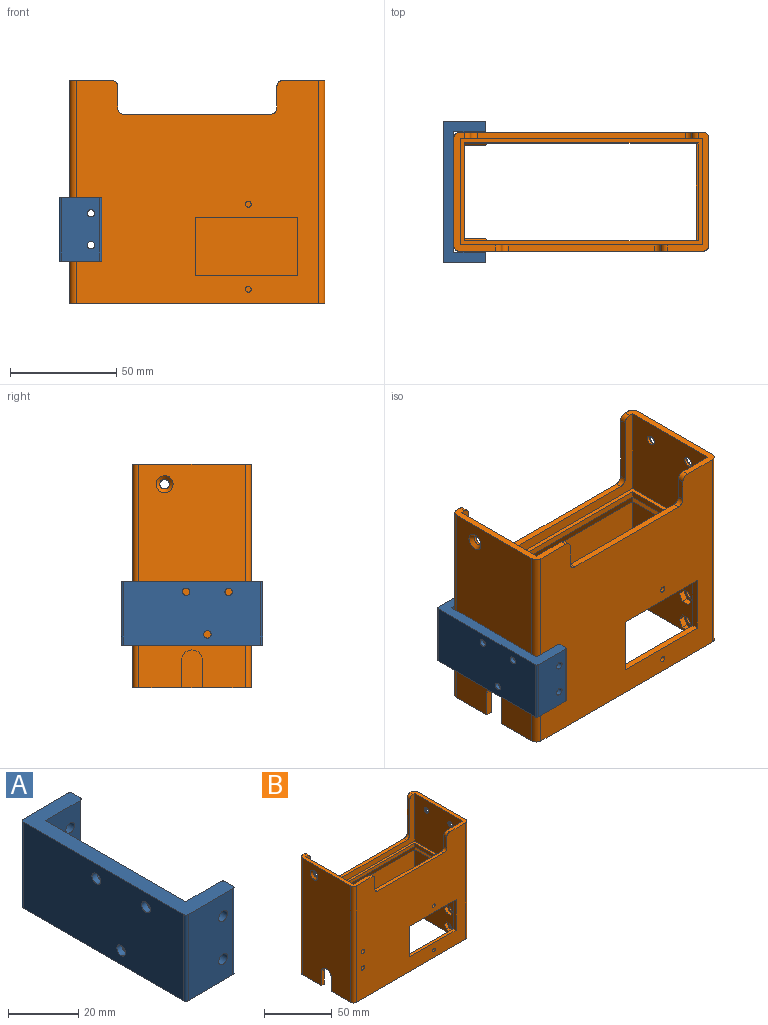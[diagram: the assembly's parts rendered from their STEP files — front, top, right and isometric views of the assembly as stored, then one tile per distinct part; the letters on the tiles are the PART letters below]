
ASSEMBLY  parts=2 mates=1
PART A: 44 faces, bbox 20x66.5x30 mm
  f0: cylinder r=1.75mm len=3.5mm, axis (-1,0,0), area 22mm2, adj f7,f27
  f1: cylinder r=1.75mm len=3.5mm, axis (-1,0,0), area 22mm2, adj f7,f20
  f2: cylinder r=1.75mm len=3.5mm, axis (-1,0,0), area 22mm2, adj f7,f13
  f3: plane 56.5x30mm, normal (1,0,0), area 1616.4mm2, adj f4,f10,f11,f12,f14,f15,f16,f17
  f4: plane 30x14mm, normal (0,-1,0), area 400.8mm2, adj f3,f11,f12,f36,f37,f38
  f5: plane 30x3mm, normal (1,0,0), area 90mm2, adj f11,f12,f38,f39
  f6: plane 30x18mm, normal (0,1,0), area 520.8mm2, adj f11,f12,f36,f37,f39,f40
  f7: plane 64.5x30mm, normal (-1,0,0), area 1906.1mm2, adj f0,f1,f2,f11,f12,f40,f41
  f8: plane 30x18mm, normal (0,-1,0), area 520.8mm2, adj f11,f12,f34,f35,f41,f42
  f9: plane 30x3mm, normal (1,0,0), area 90mm2, adj f11,f12,f42,f43
  f10: plane 30x14mm, normal (0,1,0), area 400.8mm2, adj f3,f11,f12,f34,f35,f43
  f11: plane 66.5x20mm, normal (0,0,1), area 481.2mm2, adj f3,f4,f5,f6,f7,f8,f9,f10
  f12: plane 66.5x20mm, normal (0,0,-1), area 481.2mm2, adj f3,f4,f5,f6,f7,f8,f9,f10
  f13: plane 6.35x5.5mm, normal (1,0,0), area 16.6mm2, adj f2,f14,f15,f16,f17,f18,f19
  f14: plane 3x2.75mm, normal (0,-0.87,-0.5), area 9.5mm2, adj f3,f13,f15,f19
  f15: plane 3.18x3mm, normal (0,0,-1), area 9.5mm2, adj f3,f13,f14,f16
  f16: plane 3x2.75mm, normal (0,0.87,-0.5), area 9.5mm2, adj f3,f13,f15,f17
  f17: plane 3x2.75mm, normal (0,0.87,0.5), area 9.5mm2, adj f3,f13,f16,f18
  f18: plane 3.18x3mm, normal (0,0,1), area 9.5mm2, adj f3,f13,f17,f19
  f19: plane 3x2.75mm, normal (0,-0.87,0.5), area 9.5mm2, adj f3,f13,f14,f18
  f20: plane 6.35x5.5mm, normal (1,0,0), area 16.6mm2, adj f1,f21,f22,f23,f24,f25,f26
  f21: plane 3x2.75mm, normal (0,-0.87,-0.5), area 9.5mm2, adj f3,f20,f22,f26
  f22: plane 3.18x3mm, normal (0,0,-1), area 9.5mm2, adj f3,f20,f21,f23
  f23: plane 3x2.75mm, normal (0,0.87,-0.5), area 9.5mm2, adj f3,f20,f22,f24
  f24: plane 3x2.75mm, normal (0,0.87,0.5), area 9.5mm2, adj f3,f20,f23,f25
  f25: plane 3.18x3mm, normal (0,0,1), area 9.5mm2, adj f3,f20,f24,f26
  f26: plane 3x2.75mm, normal (0,-0.87,0.5), area 9.5mm2, adj f3,f20,f21,f25
  f27: plane 6.35x5.5mm, normal (1,0,0), area 16.6mm2, adj f0,f28,f29,f30,f31,f32,f33
  f28: plane 3x2.75mm, normal (0,-0.87,-0.5), area 9.5mm2, adj f3,f27,f29,f33
  f29: plane 3.18x3mm, normal (0,0,-1), area 9.5mm2, adj f3,f27,f28,f30
  f30: plane 3x2.75mm, normal (0,0.87,-0.5), area 9.5mm2, adj f3,f27,f29,f31
  f31: plane 3x2.75mm, normal (0,0.87,0.5), area 9.5mm2, adj f3,f27,f30,f32
  f32: plane 3.18x3mm, normal (0,0,1), area 9.5mm2, adj f3,f27,f31,f33
  f33: plane 3x2.75mm, normal (0,-0.87,0.5), area 9.5mm2, adj f3,f27,f28,f32
  f34: cylinder r=1.75mm len=5mm, axis (0,-1,0), area 55mm2, adj f8,f10
  f35: cylinder r=1.75mm len=5mm, axis (0,-1,0), area 55mm2, adj f8,f10
  f36: cylinder r=1.75mm len=5mm, axis (0,-1,0), area 55mm2, adj f4,f6
  f37: cylinder r=1.75mm len=5mm, axis (0,-1,0), area 55mm2, adj f4,f6
  f38: cylinder r=1mm len=30mm, axis (0,0,-1), area 47.1mm2, adj f4,f5,f11,f12
  f39: cylinder r=1mm len=30mm, axis (0,0,1), area 47.1mm2, adj f5,f6,f11,f12
  f40: cylinder r=1mm len=30mm, axis (0,0,-1), area 47.1mm2, adj f6,f7,f11,f12
  f41: cylinder r=1mm len=30mm, axis (0,0,1), area 47.1mm2, adj f7,f8,f11,f12
  f42: cylinder r=1mm len=30mm, axis (0,0,1), area 47.1mm2, adj f8,f9,f11,f12
  f43: cylinder r=1mm len=30mm, axis (0,0,-1), area 47.1mm2, adj f9,f10,f11,f12
PART B: 131 faces, bbox 120x56x105 mm
  f0: cylinder r=2.25mm len=4.5mm, axis (1,0,0), area 42.4mm2, adj f25,f130
  f1: cylinder r=2.25mm len=4.5mm, axis (1,0,0), area 42.4mm2, adj f25,f123
  f2: cylinder r=2.25mm len=4.5mm, axis (1,0,0), area 42.4mm2, adj f25,f116
  f3: cylinder r=2.25mm len=4.5mm, axis (1,0,0), area 42.4mm2, adj f25,f109
  f4: cylinder r=1.75mm len=3.5mm, axis (0,-1,0), area 33mm2, adj f17,f96
  f5: cylinder r=1.75mm len=3.5mm, axis (0,-1,0), area 33mm2, adj f17,f89
  f6: cylinder r=1.75mm len=3.5mm, axis (0,-1,0), area 33mm2, adj f16,f82
  f7: cylinder r=1.75mm len=3.5mm, axis (0,-1,0), area 33mm2, adj f16,f75
  f8: plane 50x24.42mm, normal (-1,0,0), area 1220.9mm2, adj f9,f11,f21,f68
  f9: plane 114x54.42mm, normal (0,1,0), area 4032.1mm2, adj f8,f10,f26,f29,f32,f33,f34,f35
  f10: plane 54.42x50mm, normal (1,0,0), area 2263.6mm2, adj f9,f11,f18,f26,f46,f47,f48,f65
  f11: plane 114x54.42mm, normal (0,-1,0), area 5334.8mm2, adj f8,f10,f26,f31,f67,f68,f97,f98
  f12: plane 105x50mm, normal (-1,0,0), area 5033.4mm2, adj f15,f26,f46,f47,f48,f52,f62,f63
  f13: plane 56x19.6mm, normal (0,0,1), area 219.9mm2, adj f14,f16,f17,f22,f24,f25,f56,f57
  f14: plane 114x43mm, normal (0,1,0), area 3705.2mm2, adj f13,f15,f22,f23,f27,f41,f42,f43
  f15: plane 56x19.6mm, normal (0,0,1), area 219.9mm2, adj f12,f14,f16,f17,f23,f24,f53,f60
  f16: plane 114x105mm, normal (0,1,0), area 7866mm2, adj f6,f7,f13,f15,f26,f38,f39,f40
  f17: plane 114x105mm, normal (0,-1,0), area 9422.5mm2, adj f4,f5,f13,f15,f26,f32,f33,f34
  f18: plane 50x4.58mm, normal (0.92,0,-0.4), area 240mm2, adj f10,f19,f29,f31
  f19: plane 46x3mm, normal (1,0,0), area 138mm2, adj f18,f27,f28,f30
  f20: plane 46x3mm, normal (-1,0,0), area 138mm2, adj f21,f27,f28,f30
  f21: plane 50x4.58mm, normal (-0.92,0,-0.4), area 240mm2, adj f8,f20,f29,f31
  f22: plane 50x43mm, normal (-1,0,0), area 2118.2mm2, adj f13,f14,f24,f27,f44,f45
  f23: plane 50x43mm, normal (1,0,0), area 2134.1mm2, adj f14,f15,f24,f27,f49
  f24: plane 114x43mm, normal (0,-1,0), area 950mm2, adj f13,f15,f22,f23,f27,f38,f39,f40
  f25: plane 105x50mm, normal (1,0,0), area 5085.9mm2, adj f0,f1,f2,f3,f13,f26,f50,f51
  f26: plane 120x56mm, normal (0,0,-1), area 1213.3mm2, adj f9,f10,f11,f12,f16,f17,f25,f47
  f27: plane 114x50mm, normal (0,0,1), area 640mm2, adj f14,f19,f20,f22,f23,f24,f28,f30
  f28: plane 110x3mm, normal (0,1,0), area 330mm2, adj f19,f20,f27,f29
  f29: plane 114x4.58mm, normal (0,0.92,-0.4), area 560mm2, adj f9,f18,f21,f28
  f30: plane 110x3mm, normal (0,-1,0), area 330mm2, adj f19,f20,f27,f31
  f31: plane 114x4.58mm, normal (0,-0.92,-0.4), area 560mm2, adj f11,f18,f21,f30
  f32: plane 48x3mm, normal (0,0,1), area 144mm2, adj f9,f17,f33,f35
  f33: plane 27.5x3mm, normal (-1,0,0), area 82.5mm2, adj f9,f17,f32,f34
  f34: plane 48x3mm, normal (0,0,-1), area 144mm2, adj f9,f17,f33,f35
  f35: plane 27.5x3mm, normal (1,0,0), area 82.5mm2, adj f9,f17,f32,f34
  f36: cylinder r=1.35mm len=3mm, axis (0,-1,0), area 25.4mm2, adj f9,f17
  f37: cylinder r=1.35mm len=3mm, axis (0,-1,0), area 25.4mm2, adj f9,f17
  f38: plane 32x3mm, normal (-1,0,0), area 96mm2, adj f16,f24,f57,f58
  f39: plane 98x3mm, normal (0,0,1), area 294mm2, adj f16,f24,f58,f59
  f40: plane 32x3mm, normal (1,0,0), area 96mm2, adj f16,f24,f59,f60
  f41: plane 10x3mm, normal (1,0,0), area 30mm2, adj f14,f17,f53,f54
  f42: plane 68.8x3mm, normal (0,0,1), area 206.4mm2, adj f14,f17,f54,f55
  f43: plane 10x3mm, normal (-1,0,0), area 30mm2, adj f14,f17,f55,f56
  f44: cylinder r=2.25mm len=4.5mm, axis (1,0,0), area 17.7mm2, adj f22,f51
  f45: cylinder r=2.25mm len=4.5mm, axis (1,0,0), area 17.7mm2, adj f22,f50
  f46: cylinder r=5mm len=10mm, axis (-1,0,0), area 47.1mm2, adj f10,f12,f47,f48
  f47: plane 12.7x3mm, normal (0,-1,0), area 38.1mm2, adj f10,f12,f26,f46
  f48: plane 12.7x3mm, normal (0,1,0), area 38.1mm2, adj f10,f12,f26,f46
  f49: cylinder r=2.25mm len=4.5mm, axis (-1,0,0), area 17.7mm2, adj f23,f52
  f50: cone r=2.25mm half-angle=45deg, axis (1,0,0), area 48.6mm2, adj f25,f45
  f51: cone r=2.25mm half-angle=45deg, axis (1,0,0), area 48.6mm2, adj f25,f44
  f52: cone r=2.25mm half-angle=45deg, axis (-1,0,0), area 48.6mm2, adj f12,f49
  f53: cylinder r=3mm len=3mm, axis (0,1,0), area 14.1mm2, adj f14,f15,f17,f41
  f54: cylinder r=3mm len=3mm, axis (0,1,0), area 14.1mm2, adj f14,f17,f41,f42
  f55: cylinder r=3mm len=3mm, axis (0,-1,0), area 14.1mm2, adj f14,f17,f42,f43
  f56: cylinder r=3mm len=3mm, axis (0,-1,0), area 14.1mm2, adj f13,f14,f17,f43
  f57: cylinder r=3mm len=3mm, axis (0,-1,0), area 14.1mm2, adj f13,f16,f24,f38
  f58: cylinder r=3mm len=3mm, axis (0,-1,0), area 14.1mm2, adj f16,f24,f38,f39
  f59: cylinder r=3mm len=3mm, axis (0,1,0), area 14.1mm2, adj f16,f24,f39,f40
  f60: cylinder r=3mm len=3mm, axis (0,1,0), area 14.1mm2, adj f15,f16,f24,f40
  f61: cylinder r=3mm len=105mm, axis (0,0,1), area 494.8mm2, adj f13,f16,f25,f26
  f62: cylinder r=3mm len=105mm, axis (0,0,-1), area 494.8mm2, adj f12,f15,f16,f26
  f63: cylinder r=3mm len=105mm, axis (0,0,1), area 494.8mm2, adj f12,f15,f17,f26
  f64: cylinder r=3mm len=105mm, axis (0,0,-1), area 494.8mm2, adj f13,f17,f25,f26
  f65: plane 47x12mm, normal (0,-1,0), area 445.2mm2, adj f10,f26,f69,f70,f71,f72,f73,f74
  f66: plane 47x12mm, normal (0,1,0), area 511.6mm2, adj f10,f26,f83,f84,f85,f86,f87,f88
  f67: plane 50x30mm, normal (-1,0,0), area 1320.4mm2, adj f9,f11,f26,f68,f103,f104,f105,f106
  f68: plane 50x3mm, normal (0,0,1), area 150mm2, adj f8,f9,f11,f67
  f69: plane 3x2.75mm, normal (0.87,0,0.5), area 9.5mm2, adj f65,f70,f74,f75
  f70: plane 3.18x3mm, normal (0,0,1), area 9.5mm2, adj f65,f69,f71,f75
  f71: plane 3x2.75mm, normal (-0.87,0,0.5), area 9.5mm2, adj f65,f70,f72,f75
  f72: plane 3x2.75mm, normal (-0.87,0,-0.5), area 9.5mm2, adj f65,f71,f73,f75
  f73: plane 3.18x3mm, normal (0,0,-1), area 9.5mm2, adj f65,f72,f74,f75
  f74: plane 3x2.75mm, normal (0.87,0,-0.5), area 9.5mm2, adj f65,f69,f73,f75
  f75: plane 6.35x5.5mm, normal (0,-1,0), area 16.6mm2, adj f7,f69,f70,f71,f72,f73,f74
  f76: plane 3x2.75mm, normal (0.87,0,0.5), area 9.5mm2, adj f65,f77,f81,f82
  f77: plane 3.18x3mm, normal (0,0,1), area 9.5mm2, adj f65,f76,f78,f82
  f78: plane 3x2.75mm, normal (-0.87,0,0.5), area 9.5mm2, adj f65,f77,f79,f82
  f79: plane 3x2.75mm, normal (-0.87,0,-0.5), area 9.5mm2, adj f65,f78,f80,f82
  f80: plane 3.18x3mm, normal (0,0,-1), area 9.5mm2, adj f65,f79,f81,f82
  f81: plane 3x2.75mm, normal (0.87,0,-0.5), area 9.5mm2, adj f65,f76,f80,f82
  f82: plane 6.35x5.5mm, normal (0,-1,0), area 16.6mm2, adj f6,f76,f77,f78,f79,f80,f81
  f83: plane 3x2.75mm, normal (-0.87,0,0.5), area 9.5mm2, adj f66,f84,f88,f89
  f84: plane 3.18x3mm, normal (0,0,1), area 9.5mm2, adj f66,f83,f85,f89
  f85: plane 3x2.75mm, normal (0.87,0,0.5), area 9.5mm2, adj f66,f84,f86,f89
  f86: plane 3x2.75mm, normal (0.87,0,-0.5), area 9.5mm2, adj f66,f85,f87,f89
  f87: plane 3.18x3mm, normal (0,0,-1), area 9.5mm2, adj f66,f86,f88,f89
  f88: plane 3x2.75mm, normal (-0.87,0,-0.5), area 9.5mm2, adj f66,f83,f87,f89
  f89: plane 6.35x5.5mm, normal (0,1,0), area 16.6mm2, adj f5,f83,f84,f85,f86,f87,f88
  f90: plane 3x2.75mm, normal (-0.87,0,0.5), area 9.5mm2, adj f66,f91,f95,f96
  f91: plane 3.18x3mm, normal (0,0,1), area 9.5mm2, adj f66,f90,f92,f96
  f92: plane 3x2.75mm, normal (0.87,0,0.5), area 9.5mm2, adj f66,f91,f93,f96
  f93: plane 3x2.75mm, normal (0.87,0,-0.5), area 9.5mm2, adj f66,f92,f94,f96
  f94: plane 3.18x3mm, normal (0,0,-1), area 9.5mm2, adj f66,f93,f95,f96
  f95: plane 3x2.75mm, normal (-0.87,0,-0.5), area 9.5mm2, adj f66,f90,f94,f96
  f96: plane 6.35x5.5mm, normal (0,1,0), area 16.6mm2, adj f4,f90,f91,f92,f93,f94,f95
  f97: cylinder r=6.5mm len=13mm, axis (0,1,0), area 193mm2, adj f11,f16,f65,f98,f102
  f98: plane 4.23x3mm, normal (0.71,-0.71,0), area 15.9mm2, adj f11,f26,f65,f97
  f99: plane 15x3mm, normal (0,0.71,0.71), area 57.3mm2, adj f9,f10,f66,f100
  f100: plane 50x3mm, normal (0.71,0.71,0), area 205.8mm2, adj f9,f26,f66,f99
  f101: plane 15x3mm, normal (0,-0.71,0.71), area 57.3mm2, adj f10,f11,f65,f102
  f102: plane 34.23x3mm, normal (0.71,-0.71,0), area 136.8mm2, adj f11,f65,f97,f101
  f103: plane 3.6x3mm, normal (0,0.87,-0.5), area 12.5mm2, adj f67,f104,f108,f109
  f104: plane 4.16x3mm, normal (0,0,-1), area 12.5mm2, adj f67,f103,f105,f109
  f105: plane 3.6x3mm, normal (0,-0.87,-0.5), area 12.5mm2, adj f67,f104,f106,f109
  f106: plane 3.6x3mm, normal (0,-0.87,0.5), area 12.5mm2, adj f67,f105,f107,f109
  f107: plane 4.16x3mm, normal (0,0,1), area 12.5mm2, adj f67,f106,f108,f109
  f108: plane 3.6x3mm, normal (0,0.87,0.5), area 12.5mm2, adj f67,f103,f107,f109
  f109: plane 8.31x7.2mm, normal (-1,0,0), area 29mm2, adj f3,f103,f104,f105,f106,f107,f108
  f110: plane 3.6x3mm, normal (0,0.87,-0.5), area 12.5mm2, adj f67,f111,f115,f116
  f111: plane 4.16x3mm, normal (0,0,-1), area 12.5mm2, adj f67,f110,f112,f116
  f112: plane 3.6x3mm, normal (0,-0.87,-0.5), area 12.5mm2, adj f67,f111,f113,f116
  f113: plane 3.6x3mm, normal (0,-0.87,0.5), area 12.5mm2, adj f67,f112,f114,f116
  f114: plane 4.16x3mm, normal (0,0,1), area 12.5mm2, adj f67,f113,f115,f116
  f115: plane 3.6x3mm, normal (0,0.87,0.5), area 12.5mm2, adj f67,f110,f114,f116
  f116: plane 8.31x7.2mm, normal (-1,0,0), area 29mm2, adj f2,f110,f111,f112,f113,f114,f115
  f117: plane 3.6x3mm, normal (0,0.87,-0.5), area 12.5mm2, adj f67,f118,f122,f123
  f118: plane 4.16x3mm, normal (0,0,-1), area 12.5mm2, adj f67,f117,f119,f123
  f119: plane 3.6x3mm, normal (0,-0.87,-0.5), area 12.5mm2, adj f67,f118,f120,f123
  f120: plane 3.6x3mm, normal (0,-0.87,0.5), area 12.5mm2, adj f67,f119,f121,f123
  f121: plane 4.16x3mm, normal (0,0,1), area 12.5mm2, adj f67,f120,f122,f123
  f122: plane 3.6x3mm, normal (0,0.87,0.5), area 12.5mm2, adj f67,f117,f121,f123
  f123: plane 8.31x7.2mm, normal (-1,0,0), area 29mm2, adj f1,f117,f118,f119,f120,f121,f122
  f124: plane 3.6x3mm, normal (0,0.87,-0.5), area 12.5mm2, adj f67,f125,f129,f130
  f125: plane 4.16x3mm, normal (0,0,-1), area 12.5mm2, adj f67,f124,f126,f130
  f126: plane 3.6x3mm, normal (0,-0.87,-0.5), area 12.5mm2, adj f67,f125,f127,f130
  f127: plane 3.6x3mm, normal (0,-0.87,0.5), area 12.5mm2, adj f67,f126,f128,f130
  f128: plane 4.16x3mm, normal (0,0,1), area 12.5mm2, adj f67,f127,f129,f130
  f129: plane 3.6x3mm, normal (0,0.87,0.5), area 12.5mm2, adj f67,f124,f128,f130
  f130: plane 8.31x7.2mm, normal (-1,0,0), area 29mm2, adj f0,f124,f125,f126,f127,f128,f129
PLACE A t=(49.68,-0.25,20.42)mm
PLACE B t=(15.35,0,0.42)mm fixed
MATE fastened A.f35 <-> B.f4  axis (0,1,0) through (-34.65,-28.25,42.92)mm
